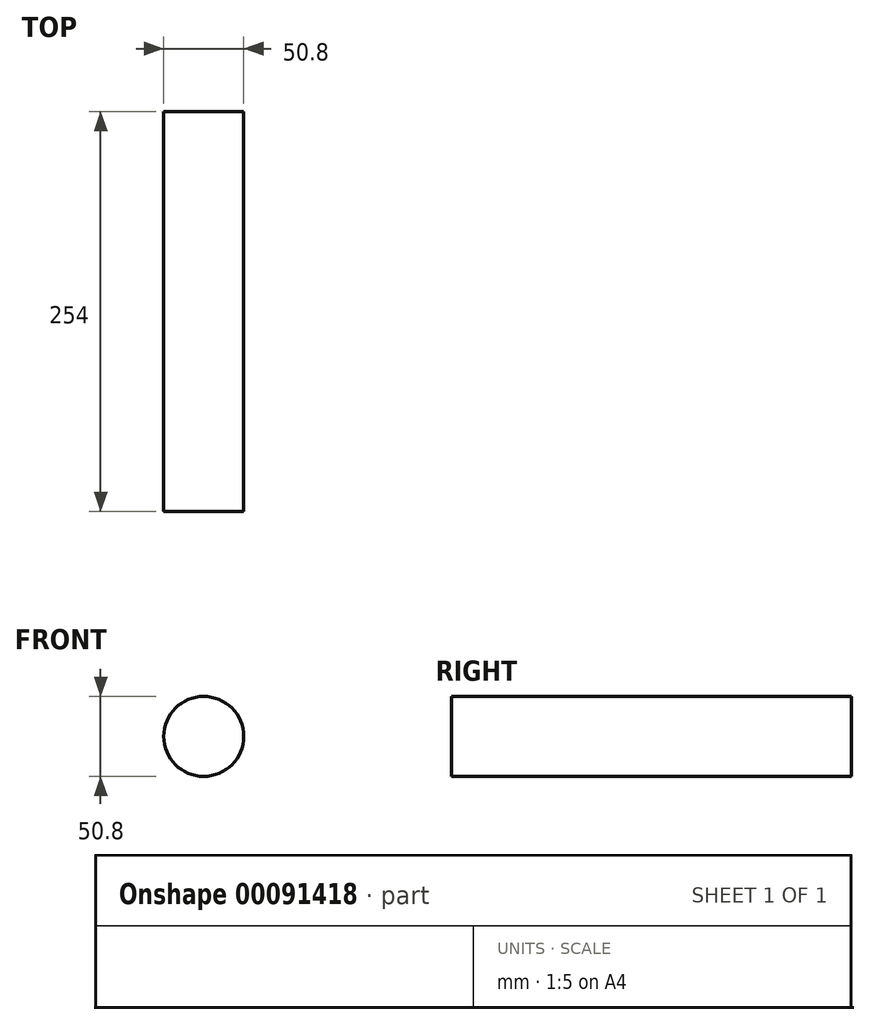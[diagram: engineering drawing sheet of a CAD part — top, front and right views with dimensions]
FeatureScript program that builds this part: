
annotation { "Feature Type Name" : "Feature", "Feature Type Description" : "" }
export const myFeature = defineFeature(function(context is Context, id is Id, definition is map)
    precondition{}
    {
        {
            var Q0;
            Q0=qCreatedBy(makeId("Front.planeOp"),FACE);
            var sketch = newSketch(context, id + "F0", { "sketchPlane" : qUnion([Q0])});
            skCircle(sketch, "E0", {"center": v(0, 0) * mm, "radius": 25.4 * mm});
            skSolve(sketch);
        }
        {
            var Q0;
            Q0 = qSketchRegion(id + "F0", true);
            extrude(context, id + "F1", {"entities" : qUnion([Q0]), "endBound" : BoundingType.SYMMETRIC, "depth" : 254 * mm});
        }
    });
